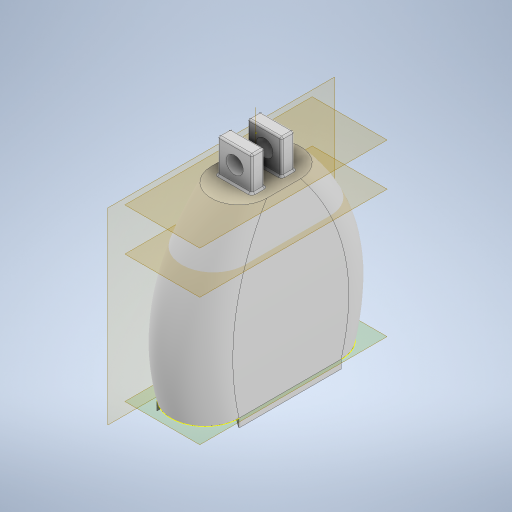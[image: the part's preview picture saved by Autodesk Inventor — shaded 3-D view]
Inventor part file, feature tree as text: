
AUTODESK INVENTOR PART (.ipt)
format: ipt  version: 2023 (Build 270158000, 158)  size: 586,240 bytes
history: native  units: mm
features: sketch x19, extrude x7, plane x4, fillet x2, chamfer x2, mirror x2, loft x1, shell x1, projected_geometry x1
ambient origin geometry x8: Origin, YZ Plane, XZ Plane, XY Plane, X Axis, Y Axis, Z Axis, Center Point
bodies: Solid1 (feature_tree)
feature tree (39):
  sketch  "Sketch1"  dims[d0=120.0mm d1=80.0mm d2=20.0mm]
  plane  "Work Plane1"
  sketch  "Sketch2"  dims[d3=200.0mm d4=40.0mm]
  plane  "Work Plane2"
  sketch  "Sketch3"  dims[d5=65.0mm d6=150.0mm]
  plane  "Work Plane3"
  loft  "Loft1"
  shell  "Shell1"  Thickness=20.0mm
  sketch  "Sketch4"  dims[d7=100.0mm d8=75.0mm]
  plane  "Work Plane4"
  extrude  "Extrusion1"  Depth=40.0mm
  sketch  "Sketch10"  dims[d15=3.0mm]
  extrude  "Extrusion2"  Depth=150.0mm
  sketch  "Sketch12"  dims[d22=40.0mm]
  extrude  "Extrusion3"  Depth=75.0mm
  extrude  "Extrusion4"  TaperAngle=0.0deg  [1 undecoded]
  fillet  "Fillet1"  [1 undecoded]
  chamfer  "Chamfer1"  Distance=10.0mm
  chamfer  "Chamfer2"  Distance=40.0mm
  extrude  "Extrusion5"  Depth=20.0mm TaperAngle=0.0deg
  extrude  "Extrusion7"  Depth=20.0mm TaperAngle=0.0deg
  mirror  "Mirror2"
  mirror  "Mirror3"
  sketch  "Sketch18"  dims[d36=2.0mm d37=2.0mm d38=45.0deg d39=55.0mm]
  sketch  "Sketch19"  dims[d40=25.0mm]
  extrude  "Extrusion8"  Depth=2.0mm TaperAngle=45.0deg
  fillet  "Fillet2"  Radius=55.0mm
  sketch  "Sketch21"  dims[d42=5.0mm]
  sketch  "Sketch22"  dims[d43=5.0mm]
  sketch  "Sketch23"  dims[d44=2.0mm]
  sketch  "Sketch24"  dims[d45=2.0mm d46=10.0mm d47=0.0mm d55=4.0mm d56=5.0mm d57=4.0mm d58=50.0mm d59=0.0mm d60=3.0mm d61=10.0mm d62=0.0mm d63=20.0mm]
  sketch  "Sketch9"  dims[d9=0.0mm d10=90.0deg d11=0.0mm d12=90.0deg d13=0.0mm d14=90.0deg]
  projected_geometry  "Projected Loop1"
  sketch  "Sketch11"  dims[d19=21.0mm d20=10.0mm d21=0.0mm]
  sketch  "Sketch13"  dims[d23=50.0mm d24=40.0mm d25=0.0mm]
  sketch  "Sketch14"  dims[d26=20.0mm d27=50.0mm d28=0.0mm]
  sketch  "Sketch15"  dims[d29=20.0mm d30=40.0mm d31=0.0mm]
  sketch  "Sketch17"  dims[d32=2.0mm d33=2.0mm d34=2.0mm d35=45.0deg]
  sketch  "Sketch20"  dims[d41=12.5mm]
note: 2 required parameter values undecoded (feature->parameter linkage not recoverable at this tier; creation-order binding heuristic only, values carry confidence <= 0.55)
